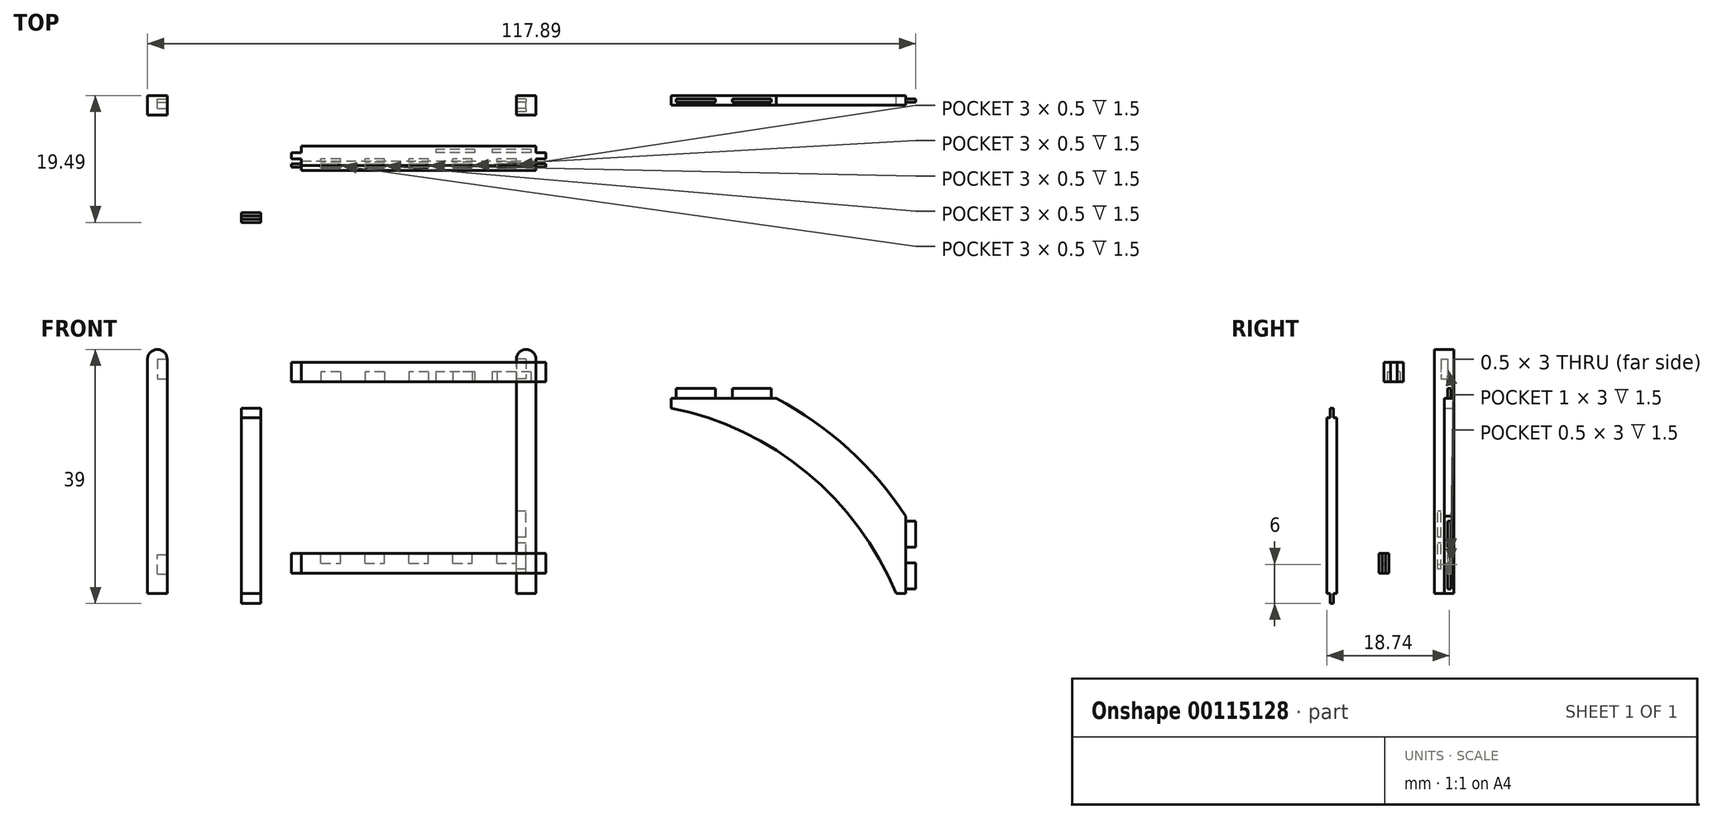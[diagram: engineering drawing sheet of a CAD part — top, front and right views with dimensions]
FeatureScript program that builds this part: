
annotation { "Feature Type Name" : "Feature", "Feature Type Description" : "" }
export const myFeature = defineFeature(function(context is Context, id is Id, definition is map)
    precondition{}
    {
        {
            var Q0;
            Q0=qCreatedBy(makeId("Front.planeOp"),FACE);
            var sketch = newSketch(context, id + "F0", { "sketchPlane" : qUnion([Q0])});
            skLineSegment(sketch, "E0.bottom", {"start": v(0, 0) * mm, "end": v(-3, 0) * mm});
            skLineSegment(sketch, "E0.left", {"start": v(0, 0) * mm, "end": v(0, 36) * mm});
            skLineSegment(sketch, "E0.right", {"start": v(-3, 0) * mm, "end": v(-3, 36) * mm});
            skArc(sketch, "E1", {"start": v(0, 36) * mm, "mid": v(-1.5, 37.5) * mm, "end": v(-3, 36) * mm});
            skSolve(sketch);
        }
        {
            var Q0;
            Q0 = qSketchRegion(id + "F0", true);
            var Q1;
            Q1=makeQuery(id+"F0.imprint","IMPRINT",FACE,{"disambiguationData":[TD([[makeQuery(id+"F0.imprint","IMPRINT",EDGE,{"derivedFrom":sQuery(id+"F0.wireOp",EDGE,"E0.bottom")}),-1.0]])]});
            extrude(context, id + "F1", {"entities" : qUnion([Q0, Q1]), "depth" : 3 * mm});
        }
        {
            var Q0;
            Q0=makeQuery(id+"F1.opExtrude","SWEPT_FACE",FACE,{"disambiguationData":[OSD([sQuery(id+"F0.wireOp",EDGE,"E0.right")])]});
            var sketch = newSketch(context, id + "F2", { "sketchPlane" : qUnion([Q0])});
            skLineSegment(sketch, "E2.bottom", {"start": v(1, 36) * mm, "end": v(2, 36) * mm});
            skLineSegment(sketch, "E2.top", {"start": v(1, 33) * mm, "end": v(2, 33) * mm});
            skLineSegment(sketch, "E2.left", {"start": v(1, 36) * mm, "end": v(1, 33) * mm});
            skLineSegment(sketch, "E2.right", {"start": v(2, 36) * mm, "end": v(2, 33) * mm});
            skSolve(sketch);
        }
        {
            var Q0;
            Q0 = qSketchRegion(id + "F2", true);
            extrude(context, id + "F3", {"entities" : qUnion([Q0]), "operationType" : NewBodyOperationType.REMOVE, "oppositeDirection" : true, "depth" : 1.5 * mm});
        }
        {
            var Q0;
            Q0=makeQuery(id+"F1.opExtrude","SWEPT_FACE",FACE,{"disambiguationData":[OSD([sQuery(id+"F0.wireOp",EDGE,"E0.right")])]});
            var sketch = newSketch(context, id + "F4", { "sketchPlane" : qUnion([Q0])});
            skLineSegment(sketch, "E3.bottom", {"start": v(0.5, 3) * mm, "end": v(1, 3) * mm});
            skLineSegment(sketch, "E3.top", {"start": v(0.5, 6) * mm, "end": v(1, 6) * mm});
            skLineSegment(sketch, "E3.left", {"start": v(0.5, 3) * mm, "end": v(0.5, 6) * mm});
            skLineSegment(sketch, "E3.right", {"start": v(1, 3) * mm, "end": v(1, 6) * mm});
            skSolve(sketch);
        }
        {
            var Q0;
            Q0 = qSketchRegion(id + "F4", true);
            extrude(context, id + "F5", {"entities" : qUnion([Q0]), "operationType" : NewBodyOperationType.REMOVE, "oppositeDirection" : true, "depth" : 1.5 * mm});
        }
        {
            var Q0;
            Q0=qCreatedBy(makeId("Right.planeOp"),FACE);
            var sketch = newSketch(context, id + "F6", { "sketchPlane" : qUnion([Q0])});
            skLineSegment(sketch, "E4.bottom", {"start": v(-10.02, 3.16) * mm, "end": v(-11.52, 3.16) * mm});
            skLineSegment(sketch, "E4.top", {"start": v(-10.02, 6.16) * mm, "end": v(-11.52, 6.16) * mm});
            skLineSegment(sketch, "E4.left", {"start": v(-10.02, 3.16) * mm, "end": v(-10.02, 6.16) * mm});
            skLineSegment(sketch, "E4.right", {"start": v(-11.52, 3.16) * mm, "end": v(-11.52, 6.16) * mm});
            skSolve(sketch);
        }
        {
            var Q0;
            Q0 = qSketchRegion(id + "F6", true);
            extrude(context, id + "F7", {"entities" : qUnion([Q0]), "oppositeDirection" : true, "depth" : 36 * mm});
        }
        {
            var Q0;
            Q0=makeQuery(id+"F7.opExtrude","CAP_FACE",FACE,{"disambiguationData":[OSD([sQuery(id+"F6.wireOp",EDGE,"E4.bottom"),sQuery(id+"F6.wireOp",EDGE,"E4.top"),sQuery(id+"F6.wireOp",EDGE,"E4.left"),sQuery(id+"F6.wireOp",EDGE,"E4.right")])],"isStart":false});
            var sketch = newSketch(context, id + "F8", { "sketchPlane" : qUnion([Q0])});
            skLineSegment(sketch, "E5.bottom", {"start": v(10.52, 6.16) * mm, "end": v(11.02, 6.16) * mm});
            skLineSegment(sketch, "E5.top", {"start": v(10.52, 3.16) * mm, "end": v(11.02, 3.16) * mm});
            skLineSegment(sketch, "E5.left", {"start": v(10.52, 6.16) * mm, "end": v(10.52, 3.16) * mm});
            skLineSegment(sketch, "E5.right", {"start": v(11.02, 6.16) * mm, "end": v(11.02, 3.16) * mm});
            skSolve(sketch);
        }
        {
            var Q0;
            Q0 = qSketchRegion(id + "F8", true);
            extrude(context, id + "F9", {"entities" : qUnion([Q0]), "operationType" : NewBodyOperationType.ADD, "depth" : 1.5 * mm});
        }
        {
            var Q0;
            Q0=makeQuery(id+"F7.opExtrude","CAP_FACE",FACE,{"disambiguationData":[OSD([sQuery(id+"F6.wireOp",EDGE,"E4.bottom"),sQuery(id+"F6.wireOp",EDGE,"E4.top"),sQuery(id+"F6.wireOp",EDGE,"E4.left"),sQuery(id+"F6.wireOp",EDGE,"E4.right")])],"isStart":true});
            var sketch = newSketch(context, id + "F10", { "sketchPlane" : qUnion([Q0])});
            skLineSegment(sketch, "E6.bottom", {"start": v(-11.02, 6.16) * mm, "end": v(-10.52, 6.16) * mm});
            skLineSegment(sketch, "E6.top", {"start": v(-11.02, 3.16) * mm, "end": v(-10.52, 3.16) * mm});
            skLineSegment(sketch, "E6.left", {"start": v(-11.02, 6.16) * mm, "end": v(-11.02, 3.16) * mm});
            skLineSegment(sketch, "E6.right", {"start": v(-10.52, 6.16) * mm, "end": v(-10.52, 3.16) * mm});
            skSolve(sketch);
        }
        {
            var Q0;
            Q0 = qSketchRegion(id + "F10", true);
            extrude(context, id + "F11", {"entities" : qUnion([Q0]), "operationType" : NewBodyOperationType.ADD, "depth" : 1.5 * mm});
        }
        {
            var Q0;
            Q0=makeQuery(id+"F11.boolean.opBoolean","MERGE",FACE,{"derivedFrom":[makeQuery(id+"F9.boolean.opBoolean","MERGE",FACE,{"derivedFrom":[makeQuery(id+"F7.opExtrude","SWEPT_FACE",FACE,{"disambiguationData":[OSD([sQuery(id+"F6.wireOp",EDGE,"E4.top")])]}),makeQuery(id+"F9.opExtrude","SWEPT_FACE",FACE,{"disambiguationData":[OSD([sQuery(id+"F8.wireOp",EDGE,"E5.bottom")])]})]}),makeQuery(id+"F11.opExtrude","SWEPT_FACE",FACE,{"disambiguationData":[OSD([sQuery(id+"F10.wireOp",EDGE,"E6.bottom")])]})]});
            var sketch = newSketch(context, id + "F12", { "sketchPlane" : qUnion([Q0])});
            skLineSegment(sketch, "E7.bottom", {"start": v(-33, -11.02) * mm, "end": v(-30, -11.02) * mm});
            skLineSegment(sketch, "E7.top", {"start": v(-33, -10.52) * mm, "end": v(-30, -10.52) * mm});
            skLineSegment(sketch, "E7.left", {"start": v(-33, -11.02) * mm, "end": v(-33, -10.52) * mm});
            skLineSegment(sketch, "E7.right", {"start": v(-30, -11.02) * mm, "end": v(-30, -10.52) * mm});
            skLineSegment(sketch, "E8.1.0.0", {"start": v(-26.25, -10.52) * mm, "end": v(-23.25, -10.52) * mm});
            skLineSegment(sketch, "E8.1.0.1", {"start": v(-26.25, -11.02) * mm, "end": v(-23.25, -11.02) * mm});
            skLineSegment(sketch, "E8.1.0.2", {"start": v(-23.25, -11.02) * mm, "end": v(-23.25, -10.52) * mm});
            skLineSegment(sketch, "E8.1.0.3", {"start": v(-26.25, -11.02) * mm, "end": v(-26.25, -10.52) * mm});
            skLineSegment(sketch, "E8.2.0.0", {"start": v(-19.5, -10.52) * mm, "end": v(-16.5, -10.52) * mm});
            skLineSegment(sketch, "E8.2.0.1", {"start": v(-19.5, -11.02) * mm, "end": v(-16.5, -11.02) * mm});
            skLineSegment(sketch, "E8.2.0.2", {"start": v(-16.5, -11.02) * mm, "end": v(-16.5, -10.52) * mm});
            skLineSegment(sketch, "E8.2.0.3", {"start": v(-19.5, -11.02) * mm, "end": v(-19.5, -10.52) * mm});
            skLineSegment(sketch, "E8.direction1", {"start": v(-33, -10.52) * mm, "end": v(-26.25, -10.52) * mm, "construction": true});
            skLineSegment(sketch, "E9.0.3.0", {"start": v(-12.75, -10.52) * mm, "end": v(-9.75, -10.52) * mm});
            skLineSegment(sketch, "E9.3.3.0", {"start": v(-12.75, -11.02) * mm, "end": v(-9.75, -11.02) * mm});
            skLineSegment(sketch, "E9.6.3.0", {"start": v(-9.75, -11.02) * mm, "end": v(-9.75, -10.52) * mm});
            skLineSegment(sketch, "E9.9.3.0", {"start": v(-12.75, -11.02) * mm, "end": v(-12.75, -10.52) * mm});
            skLineSegment(sketch, "E9.0.4.0", {"start": v(-6, -10.52) * mm, "end": v(-3, -10.52) * mm});
            skLineSegment(sketch, "E9.3.4.0", {"start": v(-6, -11.02) * mm, "end": v(-3, -11.02) * mm});
            skLineSegment(sketch, "E9.6.4.0", {"start": v(-3, -11.02) * mm, "end": v(-3, -10.52) * mm});
            skLineSegment(sketch, "E9.9.4.0", {"start": v(-6, -11.02) * mm, "end": v(-6, -10.52) * mm});
            skSolve(sketch);
        }
        {
            var Q0;
            Q0 = qSketchRegion(id + "F12", true);
            extrude(context, id + "F13", {"entities" : qUnion([Q0]), "operationType" : NewBodyOperationType.REMOVE, "oppositeDirection" : true, "depth" : 1.5 * mm});
        }
        {
            var Q0;
            Q0=qCreatedBy(makeId("Right.planeOp"),FACE);
            var sketch = newSketch(context, id + "F14", { "sketchPlane" : qUnion([Q0])});
            skLineSegment(sketch, "E10.bottom", {"start": v(-7.75, 32.54) * mm, "end": v(-10.75, 32.54) * mm});
            skLineSegment(sketch, "E10.top", {"start": v(-7.75, 35.54) * mm, "end": v(-10.75, 35.54) * mm});
            skLineSegment(sketch, "E10.left", {"start": v(-7.75, 32.54) * mm, "end": v(-7.75, 35.54) * mm});
            skLineSegment(sketch, "E10.right", {"start": v(-10.75, 32.54) * mm, "end": v(-10.75, 35.54) * mm});
            skSolve(sketch);
        }
        {
            var Q0;
            Q0 = qSketchRegion(id + "F14", true);
            extrude(context, id + "F15", {"entities" : qUnion([Q0]), "oppositeDirection" : true, "depth" : 36 * mm});
        }
        {
            var Q0;
            Q0=makeQuery(id+"F15.opExtrude","CAP_FACE",FACE,{"disambiguationData":[OSD([sQuery(id+"F14.wireOp",EDGE,"E10.bottom"),sQuery(id+"F14.wireOp",EDGE,"E10.top"),sQuery(id+"F14.wireOp",EDGE,"E10.left"),sQuery(id+"F14.wireOp",EDGE,"E10.right")])],"isStart":false});
            var sketch = newSketch(context, id + "F16", { "sketchPlane" : qUnion([Q0])});
            skLineSegment(sketch, "E11.bottom", {"start": v(8.75, 35.54) * mm, "end": v(9.75, 35.54) * mm});
            skLineSegment(sketch, "E11.top", {"start": v(8.75, 32.54) * mm, "end": v(9.75, 32.54) * mm});
            skLineSegment(sketch, "E11.left", {"start": v(8.75, 35.54) * mm, "end": v(8.75, 32.54) * mm});
            skLineSegment(sketch, "E11.right", {"start": v(9.75, 35.54) * mm, "end": v(9.75, 32.54) * mm});
            skSolve(sketch);
        }
        {
            var Q0;
            Q0 = qSketchRegion(id + "F16", true);
            extrude(context, id + "F17", {"entities" : qUnion([Q0]), "operationType" : NewBodyOperationType.ADD, "depth" : 1.5 * mm});
        }
        {
            var Q0;
            Q0=makeQuery(id+"F15.opExtrude","CAP_FACE",FACE,{"disambiguationData":[OSD([sQuery(id+"F14.wireOp",EDGE,"E10.bottom"),sQuery(id+"F14.wireOp",EDGE,"E10.top"),sQuery(id+"F14.wireOp",EDGE,"E10.left"),sQuery(id+"F14.wireOp",EDGE,"E10.right")])],"isStart":true});
            var sketch = newSketch(context, id + "F18", { "sketchPlane" : qUnion([Q0])});
            skLineSegment(sketch, "E12.bottom", {"start": v(-9.75, 35.54) * mm, "end": v(-8.75, 35.54) * mm});
            skLineSegment(sketch, "E12.top", {"start": v(-9.75, 32.54) * mm, "end": v(-8.75, 32.54) * mm});
            skLineSegment(sketch, "E12.left", {"start": v(-9.75, 35.54) * mm, "end": v(-9.75, 32.54) * mm});
            skLineSegment(sketch, "E12.right", {"start": v(-8.75, 35.54) * mm, "end": v(-8.75, 32.54) * mm});
            skSolve(sketch);
        }
        {
            var Q0;
            Q0 = qSketchRegion(id + "F18", true);
            extrude(context, id + "F19", {"entities" : qUnion([Q0]), "operationType" : NewBodyOperationType.ADD, "depth" : 1.5 * mm});
        }
        {
            var Q0;
            Q0=makeQuery(id+"F19.boolean.opBoolean","MERGE",FACE,{"derivedFrom":[makeQuery(id+"F17.boolean.opBoolean","MERGE",FACE,{"derivedFrom":[makeQuery(id+"F15.opExtrude","SWEPT_FACE",FACE,{"disambiguationData":[OSD([sQuery(id+"F14.wireOp",EDGE,"E10.bottom")])]}),makeQuery(id+"F17.opExtrude","SWEPT_FACE",FACE,{"disambiguationData":[OSD([sQuery(id+"F16.wireOp",EDGE,"E11.top")])]})]}),makeQuery(id+"F19.opExtrude","SWEPT_FACE",FACE,{"disambiguationData":[OSD([sQuery(id+"F18.wireOp",EDGE,"E12.top")])]})]});
            var sketch = newSketch(context, id + "F20", { "sketchPlane" : qUnion([Q0])});
            skLineSegment(sketch, "E13.bottom", {"start": v(-3, 10.25) * mm, "end": v(-6, 10.25) * mm});
            skLineSegment(sketch, "E13.top", {"start": v(-3, 9.75) * mm, "end": v(-6, 9.75) * mm});
            skLineSegment(sketch, "E13.left", {"start": v(-3, 10.25) * mm, "end": v(-3, 9.75) * mm});
            skLineSegment(sketch, "E13.right", {"start": v(-6, 10.25) * mm, "end": v(-6, 9.75) * mm});
            skLineSegment(sketch, "E14.1.0.0", {"start": v(-9.75, 9.75) * mm, "end": v(-12.75, 9.75) * mm});
            skLineSegment(sketch, "E14.1.0.1", {"start": v(-9.75, 10.25) * mm, "end": v(-9.75, 9.75) * mm});
            skLineSegment(sketch, "E14.1.0.2", {"start": v(-9.75, 10.25) * mm, "end": v(-12.75, 10.25) * mm});
            skLineSegment(sketch, "E14.1.0.3", {"start": v(-12.75, 10.25) * mm, "end": v(-12.75, 9.75) * mm});
            skLineSegment(sketch, "E14.2.0.0", {"start": v(-16.5, 9.75) * mm, "end": v(-19.5, 9.75) * mm});
            skLineSegment(sketch, "E14.2.0.1", {"start": v(-16.5, 10.25) * mm, "end": v(-16.5, 9.75) * mm});
            skLineSegment(sketch, "E14.2.0.2", {"start": v(-16.5, 10.25) * mm, "end": v(-19.5, 10.25) * mm});
            skLineSegment(sketch, "E14.2.0.3", {"start": v(-19.5, 10.25) * mm, "end": v(-19.5, 9.75) * mm});
            skLineSegment(sketch, "E14.direction1", {"start": v(-6, 9.75) * mm, "end": v(-12.75, 9.75) * mm, "construction": true});
            skLineSegment(sketch, "E15.0.3.0", {"start": v(-23.25, 9.75) * mm, "end": v(-26.25, 9.75) * mm});
            skLineSegment(sketch, "E15.3.3.0", {"start": v(-23.25, 10.25) * mm, "end": v(-23.25, 9.75) * mm});
            skLineSegment(sketch, "E15.6.3.0", {"start": v(-23.25, 10.25) * mm, "end": v(-26.25, 10.25) * mm});
            skLineSegment(sketch, "E15.9.3.0", {"start": v(-26.25, 10.25) * mm, "end": v(-26.25, 9.75) * mm});
            skLineSegment(sketch, "E15.0.4.0", {"start": v(-30, 9.75) * mm, "end": v(-33, 9.75) * mm});
            skLineSegment(sketch, "E15.3.4.0", {"start": v(-30, 10.25) * mm, "end": v(-30, 9.75) * mm});
            skLineSegment(sketch, "E15.6.4.0", {"start": v(-30, 10.25) * mm, "end": v(-33, 10.25) * mm});
            skLineSegment(sketch, "E15.9.4.0", {"start": v(-33, 10.25) * mm, "end": v(-33, 9.75) * mm});
            skSolve(sketch);
        }
        {
            var Q0;
            Q0 = qSketchRegion(id + "F20", true);
            extrude(context, id + "F21", {"entities" : qUnion([Q0]), "operationType" : NewBodyOperationType.REMOVE, "oppositeDirection" : true, "depth" : 1.5 * mm});
        }
        {
            var Q0;
            Q0=qCreatedBy(makeId("Front.planeOp"),FACE);
            var sketch = newSketch(context, id + "F22", { "sketchPlane" : qUnion([Q0])});
            skLineSegment(sketch, "E16.bottom", {"start": v(-59.6, 0) * mm, "end": v(-56.6, 0) * mm});
            skLineSegment(sketch, "E16.left", {"start": v(-59.6, 0) * mm, "end": v(-59.6, 36) * mm});
            skLineSegment(sketch, "E16.right", {"start": v(-56.6, 0) * mm, "end": v(-56.6, 36) * mm});
            skArc(sketch, "E17", {"start": v(-56.6, 36) * mm, "mid": v(-58.1, 37.5) * mm, "end": v(-59.6, 36) * mm});
            skSolve(sketch);
        }
        {
            var Q0;
            Q0 = qSketchRegion(id + "F22", true);
            extrude(context, id + "F23", {"entities" : qUnion([Q0]), "depth" : 3 * mm});
        }
        {
            var Q0;
            Q0=makeQuery(id+"F23.opExtrude","SWEPT_FACE",FACE,{"disambiguationData":[OSD([sQuery(id+"F22.wireOp",EDGE,"E16.right")])]});
            var sketch = newSketch(context, id + "F24", { "sketchPlane" : qUnion([Q0])});
            skLineSegment(sketch, "E18.bottom", {"start": v(-2, 36) * mm, "end": v(-1, 36) * mm});
            skLineSegment(sketch, "E18.top", {"start": v(-2, 33) * mm, "end": v(-1, 33) * mm});
            skLineSegment(sketch, "E18.left", {"start": v(-2, 36) * mm, "end": v(-2, 33) * mm});
            skLineSegment(sketch, "E18.right", {"start": v(-1, 36) * mm, "end": v(-1, 33) * mm});
            skSolve(sketch);
        }
        {
            var Q0;
            Q0 = qSketchRegion(id + "F24", true);
            extrude(context, id + "F25", {"entities" : qUnion([Q0]), "operationType" : NewBodyOperationType.REMOVE, "oppositeDirection" : true, "depth" : 1.5 * mm});
        }
        {
            var Q0;
            Q0=makeQuery(id+"F23.opExtrude","SWEPT_FACE",FACE,{"disambiguationData":[OSD([sQuery(id+"F22.wireOp",EDGE,"E16.right")])]});
            var sketch = newSketch(context, id + "F26", { "sketchPlane" : qUnion([Q0])});
            skLineSegment(sketch, "E19.bottom", {"start": v(-1, 3) * mm, "end": v(-0.5, 3) * mm});
            skLineSegment(sketch, "E19.top", {"start": v(-1, 6) * mm, "end": v(-0.5, 6) * mm});
            skLineSegment(sketch, "E19.left", {"start": v(-1, 3) * mm, "end": v(-1, 6) * mm});
            skLineSegment(sketch, "E19.right", {"start": v(-0.5, 3) * mm, "end": v(-0.5, 6) * mm});
            skSolve(sketch);
        }
        {
            var Q0;
            Q0 = qSketchRegion(id + "F26", true);
            extrude(context, id + "F27", {"entities" : qUnion([Q0]), "operationType" : NewBodyOperationType.REMOVE, "oppositeDirection" : true, "depth" : 1.5 * mm});
        }
        {
            var Q0;
            Q0=qCreatedBy(makeId("Top.planeOp"),FACE);
            var sketch = newSketch(context, id + "F28", { "sketchPlane" : qUnion([Q0])});
            skLineSegment(sketch, "E20.bottom", {"start": v(-45.2, -18) * mm, "end": v(-42.2, -18) * mm});
            skLineSegment(sketch, "E20.top", {"start": v(-45.2, -19.5) * mm, "end": v(-42.2, -19.5) * mm});
            skLineSegment(sketch, "E20.left", {"start": v(-45.2, -18) * mm, "end": v(-45.2, -19.5) * mm});
            skLineSegment(sketch, "E20.right", {"start": v(-42.2, -18) * mm, "end": v(-42.2, -19.5) * mm});
            skSolve(sketch);
        }
        {
            var Q0;
            Q0 = qSketchRegion(id + "F28", true);
            extrude(context, id + "F29", {"entities" : qUnion([Q0]), "depth" : 27 * mm});
        }
        {
            var Q0;
            Q0=makeQuery(id+"F29.opExtrude","CAP_FACE",FACE,{"disambiguationData":[OSD([sQuery(id+"F28.wireOp",EDGE,"E20.bottom"),sQuery(id+"F28.wireOp",EDGE,"E20.top"),sQuery(id+"F28.wireOp",EDGE,"E20.left"),sQuery(id+"F28.wireOp",EDGE,"E20.right")])],"isStart":false});
            var sketch = newSketch(context, id + "F30", { "sketchPlane" : qUnion([Q0])});
            skLineSegment(sketch, "E21.bottom", {"start": v(-45.2, -18.5) * mm, "end": v(-42.2, -18.5) * mm});
            skLineSegment(sketch, "E21.top", {"start": v(-45.2, -19) * mm, "end": v(-42.2, -19) * mm});
            skLineSegment(sketch, "E21.left", {"start": v(-45.2, -18.5) * mm, "end": v(-45.2, -19) * mm});
            skLineSegment(sketch, "E21.right", {"start": v(-42.2, -18.5) * mm, "end": v(-42.2, -19) * mm});
            skSolve(sketch);
        }
        {
            var Q0;
            Q0 = qSketchRegion(id + "F30", true);
            extrude(context, id + "F31", {"entities" : qUnion([Q0]), "operationType" : NewBodyOperationType.ADD, "depth" : 1.5 * mm});
        }
        {
            var Q0;
            Q0=makeQuery(id+"F29.opExtrude","CAP_FACE",FACE,{"disambiguationData":[OSD([sQuery(id+"F28.wireOp",EDGE,"E20.bottom"),sQuery(id+"F28.wireOp",EDGE,"E20.top"),sQuery(id+"F28.wireOp",EDGE,"E20.left"),sQuery(id+"F28.wireOp",EDGE,"E20.right")])],"isStart":true});
            var sketch = newSketch(context, id + "F32", { "sketchPlane" : qUnion([Q0])});
            skLineSegment(sketch, "E22.bottom", {"start": v(-45.2, 19) * mm, "end": v(-42.2, 19) * mm});
            skLineSegment(sketch, "E22.top", {"start": v(-45.2, 18.5) * mm, "end": v(-42.2, 18.5) * mm});
            skLineSegment(sketch, "E22.left", {"start": v(-45.2, 19) * mm, "end": v(-45.2, 18.5) * mm});
            skLineSegment(sketch, "E22.right", {"start": v(-42.2, 19) * mm, "end": v(-42.2, 18.5) * mm});
            skSolve(sketch);
        }
        {
            var Q0;
            Q0 = qSketchRegion(id + "F32", true);
            extrude(context, id + "F33", {"entities" : qUnion([Q0]), "operationType" : NewBodyOperationType.ADD, "depth" : 1.5 * mm});
        }
        {
            var Q0;
            Q0=qCreatedBy(makeId("Front.planeOp"),FACE);
            var sketch = newSketch(context, id + "F34", { "sketchPlane" : qUnion([Q0])});
            skLineSegment(sketch, "E23", {"start": v(56.78, 0) * mm, "end": v(55.28, 0) * mm, "construction": true});
            skLineSegment(sketch, "E24", {"start": v(20.78, 30) * mm, "end": v(20.78, 28.5) * mm});
            skArc(sketch, "E25", {"start": v(55.28, 0) * mm, "mid": v(41.61, 18.6) * mm, "end": v(20.78, 28.5) * mm});
            skLineSegment(sketch, "E26", {"start": v(20.78, 30) * mm, "end": v(36.9, 30) * mm});
            skLineSegment(sketch, "E27", {"start": v(56.78, 0) * mm, "end": v(56.78, 11.9) * mm});
            skArc(sketch, "E28", {"start": v(56.78, 11.9) * mm, "mid": v(47.98, 22.2) * mm, "end": v(36.9, 30) * mm});
            skLineSegment(sketch, "E29", {"start": v(56.78, 0) * mm, "end": v(55.28, 0) * mm});
            skSolve(sketch);
        }
        {
            var Q0;
            Q0 = qSketchRegion(id + "F34", true);
            extrude(context, id + "F35", {"entities" : qUnion([Q0]), "depth" : 1.5 * mm});
        }
        {
            var Q0;
            Q0=makeQuery(id+"F35.opExtrude","SWEPT_FACE",FACE,{"disambiguationData":[OSD([sQuery(id+"F34.wireOp",EDGE,"E26")])]});
            var sketch = newSketch(context, id + "F36", { "sketchPlane" : qUnion([Q0])});
            skLineSegment(sketch, "E30.bottom", {"start": v(27.53, -0.5) * mm, "end": v(21.53, -0.5) * mm});
            skLineSegment(sketch, "E30.top", {"start": v(27.53, -1) * mm, "end": v(21.53, -1) * mm});
            skLineSegment(sketch, "E30.left", {"start": v(27.53, -0.5) * mm, "end": v(27.53, -1) * mm});
            skLineSegment(sketch, "E30.right", {"start": v(21.53, -0.5) * mm, "end": v(21.53, -1) * mm});
            skLineSegment(sketch, "E31.bottom", {"start": v(36.16, -0.5) * mm, "end": v(30.16, -0.5) * mm});
            skLineSegment(sketch, "E31.top", {"start": v(36.16, -1) * mm, "end": v(30.16, -1) * mm});
            skLineSegment(sketch, "E31.left", {"start": v(36.16, -0.5) * mm, "end": v(36.16, -1) * mm});
            skLineSegment(sketch, "E31.right", {"start": v(30.16, -0.5) * mm, "end": v(30.16, -1) * mm});
            skSolve(sketch);
        }
        {
            var Q0;
            Q0 = qSketchRegion(id + "F36", true);
            extrude(context, id + "F37", {"entities" : qUnion([Q0]), "operationType" : NewBodyOperationType.ADD, "depth" : 1.5 * mm});
        }
        {
            var Q0;
            Q0=makeQuery(id+"F35.opExtrude","SWEPT_FACE",FACE,{"disambiguationData":[OSD([sQuery(id+"F34.wireOp",EDGE,"E27")])]});
            var sketch = newSketch(context, id + "F38", { "sketchPlane" : qUnion([Q0])});
            skLineSegment(sketch, "E32.bottom", {"start": v(-0.5, 0.75) * mm, "end": v(-1, 0.75) * mm});
            skLineSegment(sketch, "E32.top", {"start": v(-0.5, 4.75) * mm, "end": v(-1, 4.75) * mm});
            skLineSegment(sketch, "E32.left", {"start": v(-0.5, 0.75) * mm, "end": v(-0.5, 4.75) * mm});
            skLineSegment(sketch, "E32.right", {"start": v(-1, 0.75) * mm, "end": v(-1, 4.75) * mm});
            skLineSegment(sketch, "E33.bottom", {"start": v(-0.5, 7.16) * mm, "end": v(-1, 7.16) * mm});
            skLineSegment(sketch, "E33.top", {"start": v(-0.5, 11.16) * mm, "end": v(-1, 11.16) * mm});
            skLineSegment(sketch, "E33.left", {"start": v(-0.5, 7.16) * mm, "end": v(-0.5, 11.16) * mm});
            skLineSegment(sketch, "E33.right", {"start": v(-1, 7.16) * mm, "end": v(-1, 11.16) * mm});
            skSolve(sketch);
        }
        {
            var Q0;
            Q0 = qSketchRegion(id + "F38", true);
            extrude(context, id + "F39", {"entities" : qUnion([Q0]), "operationType" : NewBodyOperationType.ADD, "depth" : 1.5 * mm});
        }
        {
            var Q0;
            Q0=makeQuery(id+"F1.opExtrude","SWEPT_FACE",FACE,{"disambiguationData":[OSD([sQuery(id+"F0.wireOp",EDGE,"E0.right")])]});
            var sketch = newSketch(context, id + "F40", { "sketchPlane" : qUnion([Q0])});
            skLineSegment(sketch, "E34.bottom", {"start": v(2, 3.75) * mm, "end": v(2.5, 3.75) * mm});
            skLineSegment(sketch, "E34.top", {"start": v(2, 7.75) * mm, "end": v(2.5, 7.75) * mm});
            skLineSegment(sketch, "E34.left", {"start": v(2, 3.75) * mm, "end": v(2, 7.75) * mm});
            skLineSegment(sketch, "E34.right", {"start": v(2.5, 3.75) * mm, "end": v(2.5, 7.75) * mm});
            skLineSegment(sketch, "E35.bottom", {"start": v(2, 8.66) * mm, "end": v(2.5, 8.66) * mm});
            skLineSegment(sketch, "E35.top", {"start": v(2, 12.66) * mm, "end": v(2.5, 12.66) * mm});
            skLineSegment(sketch, "E35.left", {"start": v(2, 8.66) * mm, "end": v(2, 12.66) * mm});
            skLineSegment(sketch, "E35.right", {"start": v(2.5, 8.66) * mm, "end": v(2.5, 12.66) * mm});
            skSolve(sketch);
        }
        {
            var Q0;
            Q0 = qSketchRegion(id + "F40", true);
            extrude(context, id + "F41", {"entities" : qUnion([Q0]), "operationType" : NewBodyOperationType.REMOVE, "oppositeDirection" : true, "depth" : 1.5 * mm});
        }
        {
            var Q0;
            Q0=makeQuery(id+"F19.boolean.opBoolean","MERGE",FACE,{"derivedFrom":[makeQuery(id+"F17.boolean.opBoolean","MERGE",FACE,{"derivedFrom":[makeQuery(id+"F15.opExtrude","SWEPT_FACE",FACE,{"disambiguationData":[OSD([sQuery(id+"F14.wireOp",EDGE,"E10.bottom")])]}),makeQuery(id+"F17.opExtrude","SWEPT_FACE",FACE,{"disambiguationData":[OSD([sQuery(id+"F16.wireOp",EDGE,"E11.top")])]})]}),makeQuery(id+"F19.opExtrude","SWEPT_FACE",FACE,{"disambiguationData":[OSD([sQuery(id+"F18.wireOp",EDGE,"E12.top")])]})]});
            var sketch = newSketch(context, id + "F42", { "sketchPlane" : qUnion([Q0])});
            skLineSegment(sketch, "E36.bottom", {"start": v(-0.75, 8.25) * mm, "end": v(-6.75, 8.25) * mm});
            skLineSegment(sketch, "E36.top", {"start": v(-0.75, 8.75) * mm, "end": v(-6.75, 8.75) * mm});
            skLineSegment(sketch, "E36.left", {"start": v(-0.75, 8.25) * mm, "end": v(-0.75, 8.75) * mm});
            skLineSegment(sketch, "E36.right", {"start": v(-6.75, 8.25) * mm, "end": v(-6.75, 8.75) * mm});
            skLineSegment(sketch, "E37.bottom", {"start": v(-9.38, 8.25) * mm, "end": v(-15.38, 8.25) * mm});
            skLineSegment(sketch, "E37.top", {"start": v(-9.38, 8.75) * mm, "end": v(-15.38, 8.75) * mm});
            skLineSegment(sketch, "E37.left", {"start": v(-9.38, 8.25) * mm, "end": v(-9.38, 8.75) * mm});
            skLineSegment(sketch, "E37.right", {"start": v(-15.38, 8.25) * mm, "end": v(-15.38, 8.75) * mm});
            skSolve(sketch);
        }
        {
            var Q0;
            Q0 = qSketchRegion(id + "F42", true);
            extrude(context, id + "F43", {"entities" : qUnion([Q0]), "operationType" : NewBodyOperationType.REMOVE, "oppositeDirection" : true, "depth" : 1.5 * mm});
        }
    });
